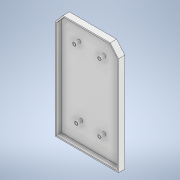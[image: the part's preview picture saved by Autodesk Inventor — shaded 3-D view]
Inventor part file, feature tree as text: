
AUTODESK INVENTOR PART (.ipt)
format: ipt  version: 2021 (Build 250183000, 183)  size: 220,160 bytes
history: native  units: in
note: dims shown in document units (in); Inventor stores cm internally (conversion verified against a paired STEP export)
features: projected_geometry x5, sketch x4, extrude x3
ambient origin geometry x8: Origin, YZ Plane, XZ Plane, XY Plane, X Axis, Y Axis, Z Axis, Center Point
bodies: Solid1 (feature_tree)
feature tree (12):
  sketch  "Sketch1"  dims[d528=0.01in d532=0.01in]
  extrude  "Extrusion1"  Depth=0.01in
  extrude  "Extrusion3"  Depth=0.25in TaperAngle=0.0deg
  extrude  "Extrusion4"  Depth=0.08in
  sketch  "Sketch2"  dims[d533=0.0625in d534=0.25in d535=0.0in]
  sketch  "Sketch4"  dims[d538=0.08in d539=0.0in d540=0.116in]
  projected_geometry  "Projected Loop2"
  sketch  "Sketch5"  dims[d541=0.16in d542=0.0in]
  projected_geometry  "Projected Loop3"
  projected_geometry  "Projected Loop4"
  projected_geometry  "Projected Loop5"
  projected_geometry  "Projected Loop6"
